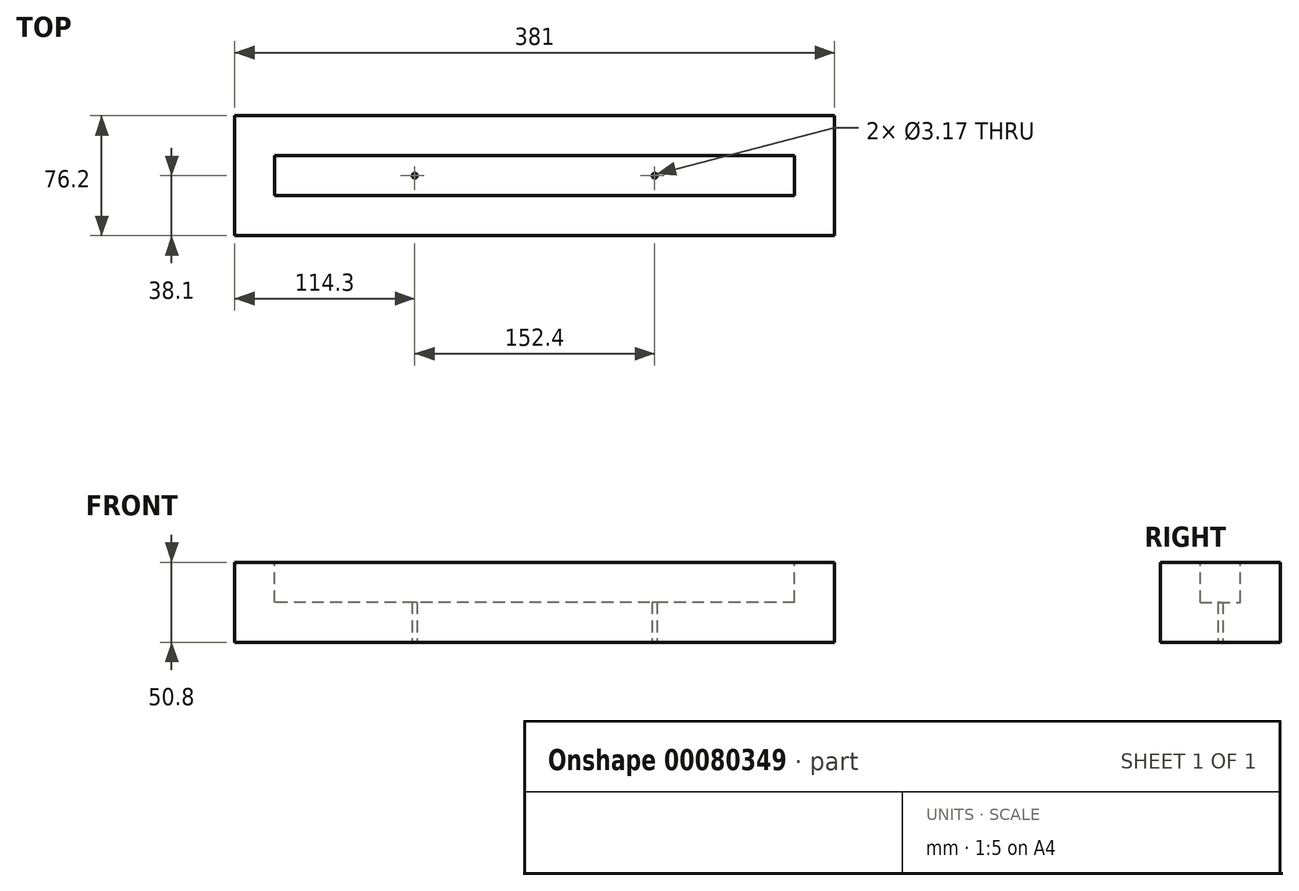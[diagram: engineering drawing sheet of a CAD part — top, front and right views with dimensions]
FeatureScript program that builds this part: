
annotation { "Feature Type Name" : "Feature", "Feature Type Description" : "" }
export const myFeature = defineFeature(function(context is Context, id is Id, definition is map)
    precondition{}
    {
        {
            var Q0;
            Q0=qCreatedBy(makeId("Top.planeOp"),FACE);
            var sketch = newSketch(context, id + "F0", { "sketchPlane" : qUnion([Q0])});
            skLineSegment(sketch, "E0.bottom", {"start": v(190.5, -38.1) * mm, "end": v(-190.5, -38.1) * mm});
            skLineSegment(sketch, "E0.top", {"start": v(190.5, 38.1) * mm, "end": v(-190.5, 38.1) * mm});
            skLineSegment(sketch, "E0.left", {"start": v(190.5, -38.1) * mm, "end": v(190.5, 38.1) * mm});
            skLineSegment(sketch, "E0.right", {"start": v(-190.5, -38.1) * mm, "end": v(-190.5, 38.1) * mm});
            skPoint(sketch, "E0.middle", {"position": v(0, 0) * mm});
            skSolve(sketch);
        }
        {
            var Q0;
            Q0 = qSketchRegion(id + "F0", true);
            extrude(context, id + "F1", {"entities" : qUnion([Q0]), "depth" : 50.8 * mm});
        }
        {
            var Q0;
            Q0=makeQuery(id+"F1.opExtrude","CAP_FACE",FACE,{"disambiguationData":[OSD([sQuery(id+"F0.wireOp",EDGE,"E0.bottom"),sQuery(id+"F0.wireOp",EDGE,"E0.top"),sQuery(id+"F0.wireOp",EDGE,"E0.left"),sQuery(id+"F0.wireOp",EDGE,"E0.right")])],"isStart":false});
            var sketch = newSketch(context, id + "F2", { "sketchPlane" : qUnion([Q0])});
            skLineSegment(sketch, "E1.bottom", {"start": v(165.1, -12.7) * mm, "end": v(-165.1, -12.7) * mm});
            skLineSegment(sketch, "E1.top", {"start": v(165.1, 12.7) * mm, "end": v(-165.1, 12.7) * mm});
            skLineSegment(sketch, "E1.left", {"start": v(165.1, -12.7) * mm, "end": v(165.1, 12.7) * mm});
            skLineSegment(sketch, "E1.right", {"start": v(-165.1, -12.7) * mm, "end": v(-165.1, 12.7) * mm});
            skPoint(sketch, "E1.middle", {"position": v(0, 0) * mm});
            skSolve(sketch);
        }
        {
            var Q0;
            Q0 = qSketchRegion(id + "F2", true);
            extrude(context, id + "F3", {"entities" : qUnion([Q0]), "operationType" : NewBodyOperationType.REMOVE, "oppositeDirection" : true, "depth" : 25.4 * mm});
        }
        {
            var Q0;
            Q0=makeQuery(id+"F1.opExtrude","CAP_FACE",FACE,{"disambiguationData":[OSD([sQuery(id+"F0.wireOp",EDGE,"E0.bottom"),sQuery(id+"F0.wireOp",EDGE,"E0.top"),sQuery(id+"F0.wireOp",EDGE,"E0.left"),sQuery(id+"F0.wireOp",EDGE,"E0.right")])],"isStart":true});
            var sketch = newSketch(context, id + "F4", { "sketchPlane" : qUnion([Q0])});
            skLineSegment(sketch, "E2.bottom", {"start": v(165.1, -12.7) * mm, "end": v(-165.1, -12.7) * mm, "construction": true});
            skLineSegment(sketch, "E2.top", {"start": v(165.1, 12.7) * mm, "end": v(-165.1, 12.7) * mm, "construction": true});
            skLineSegment(sketch, "E2.left", {"start": v(165.1, -12.7) * mm, "end": v(165.1, 12.7) * mm, "construction": true});
            skLineSegment(sketch, "E2.right", {"start": v(-165.1, -12.7) * mm, "end": v(-165.1, 12.7) * mm, "construction": true});
            skPoint(sketch, "E2.middle", {"position": v(0, 0) * mm});
            skLineSegment(sketch, "E3", {"start": v(0, 0) * mm, "end": v(-76.2, 0) * mm, "construction": true});
            skLineSegment(sketch, "E4", {"start": v(0, 0) * mm, "end": v(76.2, 0) * mm, "construction": true});
            skPoint(sketch, "E5", {"position": v(-76.2, 0) * mm});
            skPoint(sketch, "E6", {"position": v(76.2, 0) * mm});
            skSolve(sketch);
        }
        {
            var Q0;
            Q0=sQuery(id+"F4.wireOp",VERTEX,"E5");
            var Q1;
            Q1=sQuery(id+"F4.wireOp",VERTEX,"E6");
            var Q2;
            Q2=makeQuery(id+"F1.opExtrude","SWEPT_BODY",BODY,{"disambiguationData":[OSD([sQuery(id+"F0.wireOp",EDGE,"E0.bottom"),sQuery(id+"F0.wireOp",EDGE,"E0.top"),sQuery(id+"F0.wireOp",EDGE,"E0.left"),sQuery(id+"F0.wireOp",EDGE,"E0.right")])]});
            hole(context, id + "F5", {"style" : HoleStyle.SIMPLE, "endStyle" : HoleEndStyle.THROUGH, "holeDiameter" : 3.17 * mm, "locations" : qUnion([Q0, Q1]), "scope" : qUnion([Q2]), "isTappedThrough" : true});
        }
    });
